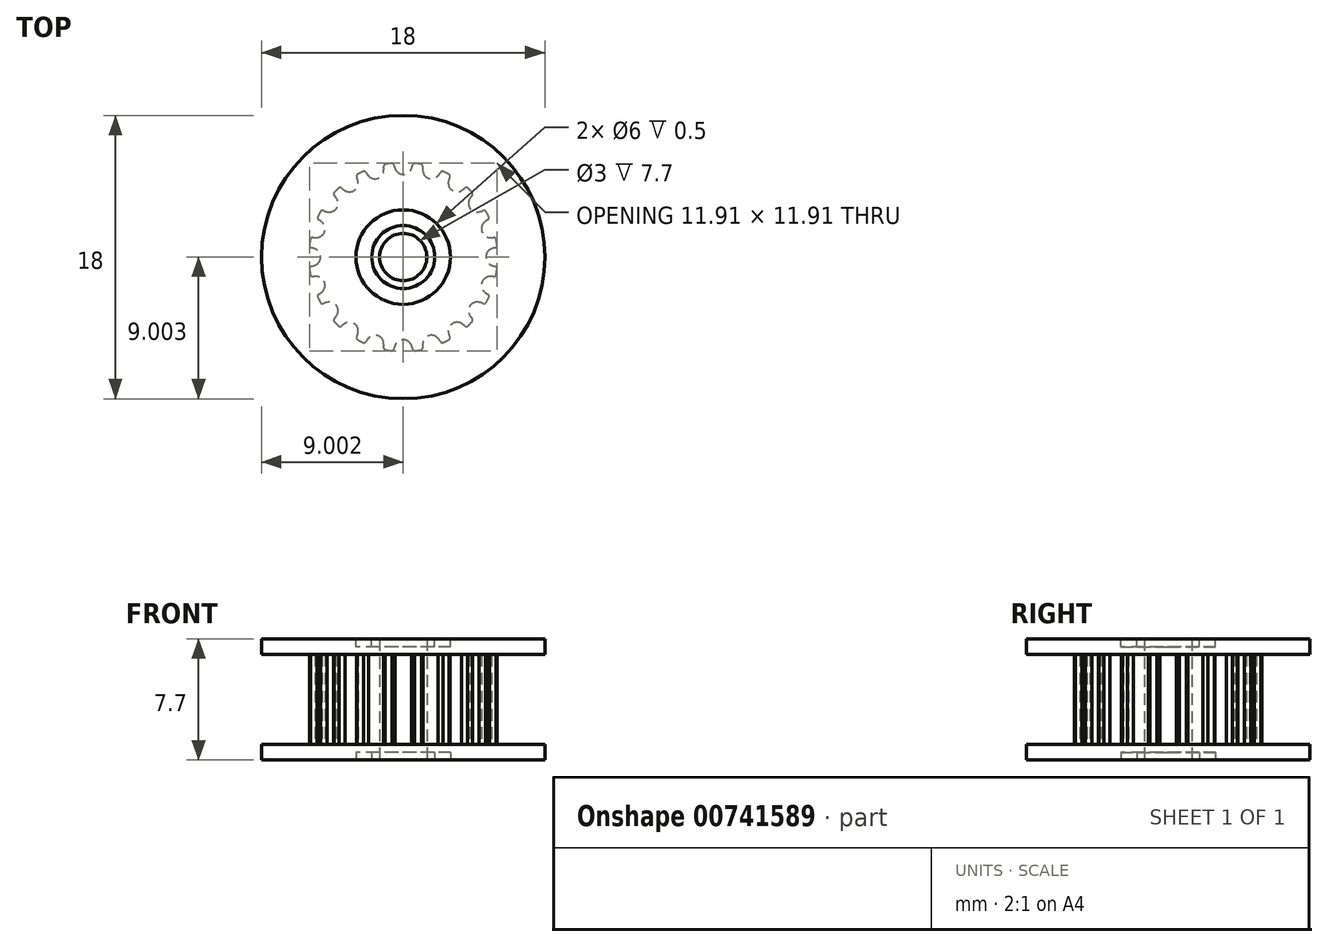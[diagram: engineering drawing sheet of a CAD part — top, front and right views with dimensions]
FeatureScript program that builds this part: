
annotation { "Feature Type Name" : "Feature", "Feature Type Description" : "" }
export const myFeature = defineFeature(function(context is Context, id is Id, definition is map)
    precondition{}
    {
        {
            var Q0;
            Q0=qCreatedBy(makeId("Top.planeOp"),FACE);
            var sketch = newSketch(context, id + "F0", { "sketchPlane" : qUnion([Q0])});
            skLineSegment(sketch, "E0", {"start": v(-17.44, 16.12) * mm, "end": v(-16.44, 16.12) * mm});
            skLineSegment(sketch, "E1", {"start": v(-16.44, 16.12) * mm, "end": v(-16.44, 16.75) * mm});
            skArc(sketch, "E2", {"start": v(-16.94, 17.19) * mm, "mid": v(-17.15, 17.42) * mm, "end": v(-17.44, 17.5) * mm});
            skArc(sketch, "E3", {"start": v(-16.85, 16.88) * mm, "mid": v(-16.88, 17.04) * mm, "end": v(-16.94, 17.19) * mm});
            skArc(sketch, "E4", {"start": v(-16.85, 16.88) * mm, "mid": v(-16.8, 16.79) * mm, "end": v(-16.7, 16.75) * mm});
            skLineSegment(sketch, "E5", {"start": v(-16.7, 16.75) * mm, "end": v(-16.44, 16.75) * mm});
            skArc(sketch, "E6.0.MirrorCS", {"start": v(-17.94, 17.19) * mm, "mid": v(-17.73, 17.42) * mm, "end": v(-17.44, 17.5) * mm});
            skArc(sketch, "E7.0.MirrorCS", {"start": v(-18.03, 16.88) * mm, "mid": v(-18, 17.04) * mm, "end": v(-17.94, 17.19) * mm});
            skArc(sketch, "E8.0.MirrorCS", {"start": v(-18.03, 16.88) * mm, "mid": v(-18.08, 16.79) * mm, "end": v(-18.18, 16.75) * mm});
            skLineSegment(sketch, "E9.0.MirrorCS", {"start": v(-18.18, 16.75) * mm, "end": v(-18.44, 16.75) * mm});
            skLineSegment(sketch, "E10.0.MirrorCS", {"start": v(-18.44, 16.12) * mm, "end": v(-18.44, 16.75) * mm});
            skLineSegment(sketch, "E11.0.MirrorCS", {"start": v(-17.44, 16.12) * mm, "end": v(-18.44, 16.12) * mm});
            skLineSegment(sketch, "E12.direction1", {"start": v(-18.44, 16.12) * mm, "end": v(-16.44, 16.12) * mm, "construction": true});
            skLineSegment(sketch, "E13", {"start": v(-18.44, 16.5) * mm, "end": v(-16.44, 16.5) * mm, "construction": true});
            skPoint(sketch, "E14", {"position": v(1.73, -6.9) * mm});
            skArc(sketch, "E15", {"start": v(2.25, -7.25) * mm, "mid": v(1.73, -6.9) * mm, "end": v(1.22, -7.25) * mm});
            skArc(sketch, "E16", {"start": v(1.22, -7.25) * mm, "mid": v(1.17, -7.37) * mm, "end": v(1.14, -7.5) * mm});
            skArc(sketch, "E17", {"start": v(2.32, -7.5) * mm, "mid": v(2.3, -7.37) * mm, "end": v(2.25, -7.25) * mm});
            skArc(sketch, "E18", {"start": v(2.45, -7.61) * mm, "mid": v(2.67, -7.58) * mm, "end": v(2.89, -7.54) * mm});
            skArc(sketch, "E19", {"start": v(2.32, -7.5) * mm, "mid": v(2.4, -7.6) * mm, "end": v(2.52, -7.6) * mm});
            skArc(sketch, "E20", {"start": v(1.14, -7.5) * mm, "mid": v(1.07, -7.6) * mm, "end": v(0.94, -7.6) * mm});
            skArc(sketch, "E21.1.0", {"start": v(3.95, -6.82) * mm, "mid": v(3.35, -6.65) * mm, "end": v(2.97, -7.14) * mm});
            skPoint(sketch, "E21.1.1", {"position": v(3.35, -6.65) * mm});
            skArc(sketch, "E21.1.2", {"start": v(2.97, -7.14) * mm, "mid": v(2.97, -7.26) * mm, "end": v(2.97, -7.39) * mm});
            skArc(sketch, "E21.1.3", {"start": v(4.1, -7.02) * mm, "mid": v(4.2, -7.1) * mm, "end": v(4.32, -7.07) * mm});
            skArc(sketch, "E21.1.4", {"start": v(2.97, -7.39) * mm, "mid": v(2.93, -7.51) * mm, "end": v(2.82, -7.56) * mm});
            skArc(sketch, "E21.1.5", {"start": v(4.1, -7.02) * mm, "mid": v(4.03, -6.92) * mm, "end": v(3.95, -6.82) * mm});
            skArc(sketch, "E22.3.2.0", {"start": v(5.44, -5.88) * mm, "mid": v(4.82, -5.9) * mm, "end": v(4.6, -6.49) * mm});
            skPoint(sketch, "E22.4.2.0", {"position": v(4.82, -5.9) * mm});
            skArc(sketch, "E22.5.2.0", {"start": v(4.6, -6.49) * mm, "mid": v(4.64, -6.6) * mm, "end": v(4.68, -6.72) * mm});
            skArc(sketch, "E22.9.2.0", {"start": v(5.64, -6.03) * mm, "mid": v(5.76, -6.07) * mm, "end": v(5.87, -6) * mm});
            skArc(sketch, "E22.13.2.0", {"start": v(4.68, -6.72) * mm, "mid": v(4.69, -6.85) * mm, "end": v(4.59, -6.93) * mm});
            skArc(sketch, "E22.17.2.0", {"start": v(5.64, -6.03) * mm, "mid": v(5.54, -5.95) * mm, "end": v(5.44, -5.88) * mm});
            skArc(sketch, "E22.3.3.0", {"start": v(6.56, -4.53) * mm, "mid": v(5.98, -4.74) * mm, "end": v(5.96, -5.36) * mm});
            skPoint(sketch, "E22.4.3.0", {"position": v(5.98, -4.74) * mm});
            skArc(sketch, "E22.5.3.0", {"start": v(5.96, -5.36) * mm, "mid": v(6.02, -5.47) * mm, "end": v(6.1, -5.56) * mm});
            skArc(sketch, "E22.9.3.0", {"start": v(6.8, -4.6) * mm, "mid": v(6.93, -4.61) * mm, "end": v(7, -4.51) * mm});
            skArc(sketch, "E22.13.3.0", {"start": v(6.1, -5.56) * mm, "mid": v(6.15, -5.69) * mm, "end": v(6.08, -5.8) * mm});
            skArc(sketch, "E22.17.3.0", {"start": v(6.8, -4.6) * mm, "mid": v(6.68, -4.56) * mm, "end": v(6.56, -4.53) * mm});
            skArc(sketch, "E22.3.4.0", {"start": v(7.21, -2.9) * mm, "mid": v(6.72, -3.28) * mm, "end": v(6.9, -3.87) * mm});
            skPoint(sketch, "E22.4.4.0", {"position": v(6.72, -3.28) * mm});
            skArc(sketch, "E22.5.4.0", {"start": v(6.9, -3.87) * mm, "mid": v(7, -3.95) * mm, "end": v(7.1, -4.02) * mm});
            skArc(sketch, "E22.9.4.0", {"start": v(7.46, -2.9) * mm, "mid": v(7.59, -2.86) * mm, "end": v(7.63, -2.74) * mm});
            skArc(sketch, "E22.13.4.0", {"start": v(7.1, -4.02) * mm, "mid": v(7.17, -4.12) * mm, "end": v(7.14, -4.25) * mm});
            skArc(sketch, "E22.17.4.0", {"start": v(7.46, -2.9) * mm, "mid": v(7.34, -2.9) * mm, "end": v(7.21, -2.9) * mm});
            skArc(sketch, "E22.3.5.0", {"start": v(7.33, -1.14) * mm, "mid": v(6.98, -1.66) * mm, "end": v(7.33, -2.17) * mm});
            skPoint(sketch, "E22.4.5.0", {"position": v(6.98, -1.66) * mm});
            skArc(sketch, "E22.5.5.0", {"start": v(7.33, -2.17) * mm, "mid": v(7.44, -2.22) * mm, "end": v(7.57, -2.25) * mm});
            skArc(sketch, "E22.9.5.0", {"start": v(7.57, -1.07) * mm, "mid": v(7.67, -1) * mm, "end": v(7.68, -0.86) * mm});
            skArc(sketch, "E22.13.5.0", {"start": v(7.57, -2.25) * mm, "mid": v(7.67, -2.32) * mm, "end": v(7.68, -2.45) * mm});
            skArc(sketch, "E22.17.5.0", {"start": v(7.57, -1.07) * mm, "mid": v(7.44, -1.1) * mm, "end": v(7.33, -1.14) * mm});
            skArc(sketch, "E22.3.6.0", {"start": v(6.9, 0.56) * mm, "mid": v(6.72, -0.03) * mm, "end": v(7.21, -0.42) * mm});
            skPoint(sketch, "E22.4.6.0", {"position": v(6.72, -0.03) * mm});
            skArc(sketch, "E22.5.6.0", {"start": v(7.21, -0.42) * mm, "mid": v(7.34, -0.42) * mm, "end": v(7.46, -0.41) * mm});
            skArc(sketch, "E22.9.6.0", {"start": v(7.1, 0.7) * mm, "mid": v(7.17, 0.81) * mm, "end": v(7.14, 0.93) * mm});
            skArc(sketch, "E22.13.6.0", {"start": v(7.46, -0.41) * mm, "mid": v(7.59, -0.45) * mm, "end": v(7.63, -0.57) * mm});
            skArc(sketch, "E22.17.6.0", {"start": v(7.1, 0.7) * mm, "mid": v(7, 0.64) * mm, "end": v(6.9, 0.56) * mm});
            skArc(sketch, "E22.3.7.0", {"start": v(5.96, 2.05) * mm, "mid": v(5.98, 1.43) * mm, "end": v(6.56, 1.22) * mm});
            skPoint(sketch, "E22.4.7.0", {"position": v(5.98, 1.43) * mm});
            skArc(sketch, "E22.5.7.0", {"start": v(6.56, 1.22) * mm, "mid": v(6.68, 1.25) * mm, "end": v(6.8, 1.3) * mm});
            skArc(sketch, "E22.9.7.0", {"start": v(6.1, 2.25) * mm, "mid": v(6.15, 2.37) * mm, "end": v(6.08, 2.48) * mm});
            skArc(sketch, "E22.13.7.0", {"start": v(6.8, 1.3) * mm, "mid": v(6.93, 1.3) * mm, "end": v(7, 1.2) * mm});
            skArc(sketch, "E22.17.7.0", {"start": v(6.1, 2.25) * mm, "mid": v(6.02, 2.15) * mm, "end": v(5.96, 2.05) * mm});
            skArc(sketch, "E22.3.8.0", {"start": v(4.6, 3.17) * mm, "mid": v(4.82, 2.6) * mm, "end": v(5.44, 2.57) * mm});
            skPoint(sketch, "E22.4.8.0", {"position": v(4.82, 2.6) * mm});
            skArc(sketch, "E22.5.8.0", {"start": v(5.44, 2.57) * mm, "mid": v(5.54, 2.64) * mm, "end": v(5.64, 2.72) * mm});
            skArc(sketch, "E22.9.8.0", {"start": v(4.68, 3.41) * mm, "mid": v(4.69, 3.54) * mm, "end": v(4.59, 3.62) * mm});
            skArc(sketch, "E22.13.8.0", {"start": v(5.64, 2.72) * mm, "mid": v(5.76, 2.76) * mm, "end": v(5.87, 2.69) * mm});
            skArc(sketch, "E22.17.8.0", {"start": v(4.68, 3.41) * mm, "mid": v(4.64, 3.3) * mm, "end": v(4.6, 3.17) * mm});
            skArc(sketch, "E22.3.9.0", {"start": v(2.97, 3.82) * mm, "mid": v(3.35, 3.34) * mm, "end": v(3.95, 3.5) * mm});
            skPoint(sketch, "E22.4.9.0", {"position": v(3.35, 3.34) * mm});
            skArc(sketch, "E22.5.9.0", {"start": v(3.95, 3.5) * mm, "mid": v(4.03, 3.6) * mm, "end": v(4.1, 3.71) * mm});
            skArc(sketch, "E22.9.9.0", {"start": v(2.97, 4.07) * mm, "mid": v(2.93, 4.2) * mm, "end": v(2.82, 4.24) * mm});
            skArc(sketch, "E22.13.9.0", {"start": v(4.1, 3.71) * mm, "mid": v(4.2, 3.79) * mm, "end": v(4.32, 3.75) * mm});
            skArc(sketch, "E22.17.9.0", {"start": v(2.97, 4.07) * mm, "mid": v(2.97, 3.95) * mm, "end": v(2.97, 3.82) * mm});
            skArc(sketch, "E22.3.10.0", {"start": v(1.22, 3.94) * mm, "mid": v(1.73, 3.6) * mm, "end": v(2.25, 3.94) * mm});
            skPoint(sketch, "E22.4.10.0", {"position": v(1.73, 3.6) * mm});
            skArc(sketch, "E22.5.10.0", {"start": v(2.25, 3.94) * mm, "mid": v(2.3, 4.06) * mm, "end": v(2.32, 4.18) * mm});
            skArc(sketch, "E22.9.10.0", {"start": v(1.14, 4.18) * mm, "mid": v(1.07, 4.28) * mm, "end": v(0.94, 4.3) * mm});
            skArc(sketch, "E22.13.10.0", {"start": v(2.32, 4.18) * mm, "mid": v(2.4, 4.28) * mm, "end": v(2.52, 4.3) * mm});
            skArc(sketch, "E22.17.10.0", {"start": v(1.14, 4.18) * mm, "mid": v(1.17, 4.06) * mm, "end": v(1.22, 3.94) * mm});
            skArc(sketch, "E22.3.11.0", {"start": v(-0.49, 3.5) * mm, "mid": v(0.1, 3.34) * mm, "end": v(0.5, 3.82) * mm});
            skPoint(sketch, "E22.4.11.0", {"position": v(0.1, 3.34) * mm});
            skArc(sketch, "E22.5.11.0", {"start": v(0.5, 3.82) * mm, "mid": v(0.5, 3.95) * mm, "end": v(0.49, 4.07) * mm});
            skArc(sketch, "E22.9.11.0", {"start": v(-0.63, 3.71) * mm, "mid": v(-0.74, 3.79) * mm, "end": v(-0.86, 3.75) * mm});
            skArc(sketch, "E22.13.11.0", {"start": v(0.49, 4.07) * mm, "mid": v(0.53, 4.2) * mm, "end": v(0.65, 4.24) * mm});
            skArc(sketch, "E22.17.11.0", {"start": v(-0.63, 3.71) * mm, "mid": v(-0.57, 3.6) * mm, "end": v(-0.49, 3.5) * mm});
            skArc(sketch, "E22.3.12.0", {"start": v(-1.97, 2.57) * mm, "mid": v(-1.35, 2.6) * mm, "end": v(-1.14, 3.17) * mm});
            skPoint(sketch, "E22.4.12.0", {"position": v(-1.35, 2.6) * mm});
            skArc(sketch, "E22.5.12.0", {"start": v(-1.14, 3.17) * mm, "mid": v(-1.17, 3.3) * mm, "end": v(-1.22, 3.41) * mm});
            skArc(sketch, "E22.9.12.0", {"start": v(-2.18, 2.72) * mm, "mid": v(-2.3, 2.76) * mm, "end": v(-2.4, 2.69) * mm});
            skArc(sketch, "E22.13.12.0", {"start": v(-1.22, 3.41) * mm, "mid": v(-1.22, 3.54) * mm, "end": v(-1.12, 3.62) * mm});
            skArc(sketch, "E22.17.12.0", {"start": v(-2.18, 2.72) * mm, "mid": v(-2.08, 2.64) * mm, "end": v(-1.97, 2.57) * mm});
            skArc(sketch, "E22.3.13.0", {"start": v(-3.1, 1.22) * mm, "mid": v(-2.52, 1.43) * mm, "end": v(-2.5, 2.05) * mm});
            skPoint(sketch, "E22.4.13.0", {"position": v(-2.52, 1.43) * mm});
            skArc(sketch, "E22.5.13.0", {"start": v(-2.5, 2.05) * mm, "mid": v(-2.56, 2.15) * mm, "end": v(-2.64, 2.25) * mm});
            skArc(sketch, "E22.9.13.0", {"start": v(-3.34, 1.3) * mm, "mid": v(-3.46, 1.3) * mm, "end": v(-3.55, 1.2) * mm});
            skArc(sketch, "E22.13.13.0", {"start": v(-2.64, 2.25) * mm, "mid": v(-2.68, 2.37) * mm, "end": v(-2.61, 2.48) * mm});
            skArc(sketch, "E22.17.13.0", {"start": v(-3.34, 1.3) * mm, "mid": v(-3.22, 1.25) * mm, "end": v(-3.1, 1.22) * mm});
            skArc(sketch, "E22.3.14.0", {"start": v(-3.75, -0.42) * mm, "mid": v(-3.26, -0.03) * mm, "end": v(-3.43, 0.56) * mm});
            skPoint(sketch, "E22.4.14.0", {"position": v(-3.26, -0.03) * mm});
            skArc(sketch, "E22.5.14.0", {"start": v(-3.43, 0.56) * mm, "mid": v(-3.53, 0.64) * mm, "end": v(-3.64, 0.7) * mm});
            skArc(sketch, "E22.9.14.0", {"start": v(-4, -0.41) * mm, "mid": v(-4.12, -0.45) * mm, "end": v(-4.17, -0.57) * mm});
            skArc(sketch, "E22.13.14.0", {"start": v(-3.64, 0.7) * mm, "mid": v(-3.71, 0.81) * mm, "end": v(-3.68, 0.93) * mm});
            skArc(sketch, "E22.17.14.0", {"start": v(-4, -0.41) * mm, "mid": v(-3.87, -0.42) * mm, "end": v(-3.75, -0.42) * mm});
            skArc(sketch, "E22.3.15.0", {"start": v(-3.86, -2.17) * mm, "mid": v(-3.52, -1.66) * mm, "end": v(-3.86, -1.14) * mm});
            skPoint(sketch, "E22.4.15.0", {"position": v(-3.52, -1.66) * mm});
            skArc(sketch, "E22.5.15.0", {"start": v(-3.86, -1.14) * mm, "mid": v(-3.98, -1.1) * mm, "end": v(-4.1, -1.07) * mm});
            skArc(sketch, "E22.9.15.0", {"start": v(-4.1, -2.25) * mm, "mid": v(-4.2, -2.32) * mm, "end": v(-4.22, -2.45) * mm});
            skArc(sketch, "E22.13.15.0", {"start": v(-4.1, -1.07) * mm, "mid": v(-4.2, -1) * mm, "end": v(-4.22, -0.86) * mm});
            skArc(sketch, "E22.17.15.0", {"start": v(-4.1, -2.25) * mm, "mid": v(-3.98, -2.22) * mm, "end": v(-3.86, -2.17) * mm});
            skArc(sketch, "E22.3.16.0", {"start": v(-3.43, -3.87) * mm, "mid": v(-3.26, -3.28) * mm, "end": v(-3.75, -2.9) * mm});
            skPoint(sketch, "E22.4.16.0", {"position": v(-3.26, -3.28) * mm});
            skArc(sketch, "E22.5.16.0", {"start": v(-3.75, -2.9) * mm, "mid": v(-3.87, -2.9) * mm, "end": v(-4, -2.9) * mm});
            skArc(sketch, "E22.9.16.0", {"start": v(-3.64, -4.02) * mm, "mid": v(-3.71, -4.12) * mm, "end": v(-3.68, -4.25) * mm});
            skArc(sketch, "E22.13.16.0", {"start": v(-4, -2.9) * mm, "mid": v(-4.12, -2.86) * mm, "end": v(-4.17, -2.74) * mm});
            skArc(sketch, "E22.17.16.0", {"start": v(-3.64, -4.02) * mm, "mid": v(-3.53, -3.95) * mm, "end": v(-3.43, -3.87) * mm});
            skArc(sketch, "E22.3.17.0", {"start": v(-2.5, -5.36) * mm, "mid": v(-2.52, -4.74) * mm, "end": v(-3.1, -4.53) * mm});
            skPoint(sketch, "E22.4.17.0", {"position": v(-2.52, -4.74) * mm});
            skArc(sketch, "E22.5.17.0", {"start": v(-3.1, -4.53) * mm, "mid": v(-3.22, -4.56) * mm, "end": v(-3.34, -4.6) * mm});
            skArc(sketch, "E22.9.17.0", {"start": v(-2.64, -5.56) * mm, "mid": v(-2.68, -5.69) * mm, "end": v(-2.61, -5.8) * mm});
            skArc(sketch, "E22.13.17.0", {"start": v(-3.34, -4.6) * mm, "mid": v(-3.46, -4.61) * mm, "end": v(-3.55, -4.51) * mm});
            skArc(sketch, "E22.17.17.0", {"start": v(-2.64, -5.56) * mm, "mid": v(-2.56, -5.47) * mm, "end": v(-2.5, -5.36) * mm});
            skArc(sketch, "E22.3.18.0", {"start": v(-1.14, -6.49) * mm, "mid": v(-1.35, -5.9) * mm, "end": v(-1.97, -5.88) * mm});
            skPoint(sketch, "E22.4.18.0", {"position": v(-1.35, -5.9) * mm});
            skArc(sketch, "E22.5.18.0", {"start": v(-1.97, -5.88) * mm, "mid": v(-2.08, -5.95) * mm, "end": v(-2.18, -6.03) * mm});
            skArc(sketch, "E22.9.18.0", {"start": v(-1.22, -6.72) * mm, "mid": v(-1.22, -6.85) * mm, "end": v(-1.12, -6.93) * mm});
            skArc(sketch, "E22.13.18.0", {"start": v(-2.18, -6.03) * mm, "mid": v(-2.3, -6.07) * mm, "end": v(-2.4, -6) * mm});
            skArc(sketch, "E22.17.18.0", {"start": v(-1.22, -6.72) * mm, "mid": v(-1.17, -6.6) * mm, "end": v(-1.14, -6.49) * mm});
            skArc(sketch, "E22.3.19.0", {"start": v(0.5, -7.14) * mm, "mid": v(0.1, -6.65) * mm, "end": v(-0.49, -6.82) * mm});
            skPoint(sketch, "E22.4.19.0", {"position": v(0.1, -6.65) * mm});
            skArc(sketch, "E22.5.19.0", {"start": v(-0.49, -6.82) * mm, "mid": v(-0.57, -6.92) * mm, "end": v(-0.63, -7.02) * mm});
            skArc(sketch, "E22.9.19.0", {"start": v(0.49, -7.39) * mm, "mid": v(0.53, -7.51) * mm, "end": v(0.65, -7.56) * mm});
            skArc(sketch, "E22.13.19.0", {"start": v(-0.63, -7.02) * mm, "mid": v(-0.74, -7.1) * mm, "end": v(-0.86, -7.07) * mm});
            skArc(sketch, "E22.17.19.0", {"start": v(0.49, -7.39) * mm, "mid": v(0.5, -7.26) * mm, "end": v(0.5, -7.14) * mm});
            skArc(sketch, "E23.trimOffspring", {"start": v(4.26, -7.1) * mm, "mid": v(4.46, -7) * mm, "end": v(4.65, -6.9) * mm});
            skArc(sketch, "E24.trimOffspring", {"start": v(5.81, -6.05) * mm, "mid": v(5.97, -5.9) * mm, "end": v(6.13, -5.74) * mm});
            skArc(sketch, "E25.trimOffspring", {"start": v(6.97, -4.58) * mm, "mid": v(7.06, -4.41) * mm, "end": v(7.14, -4.25) * mm});
            skArc(sketch, "E26.trimOffspring", {"start": v(7.62, -2.81) * mm, "mid": v(7.66, -2.6) * mm, "end": v(7.69, -2.38) * mm});
            skArc(sketch, "E27.trimOffspring", {"start": v(7.18, 0.87) * mm, "mid": v(7.08, 1.07) * mm, "end": v(6.97, 1.26) * mm});
            skArc(sketch, "E28.trimOffspring", {"start": v(6.13, 2.43) * mm, "mid": v(5.97, 2.59) * mm, "end": v(5.81, 2.74) * mm});
            skArc(sketch, "E29.trimOffspring", {"start": v(7.69, -0.94) * mm, "mid": v(7.66, -0.72) * mm, "end": v(7.62, -0.5) * mm});
            skArc(sketch, "E30.trimOffspring", {"start": v(4.65, 3.58) * mm, "mid": v(4.46, 3.69) * mm, "end": v(4.26, 3.79) * mm});
            skArc(sketch, "E31.trimOffspring", {"start": v(2.89, 4.23) * mm, "mid": v(2.67, 4.27) * mm, "end": v(2.45, 4.3) * mm});
            skArc(sketch, "E32.trimOffspring", {"start": v(1.01, 4.3) * mm, "mid": v(0.8, 4.27) * mm, "end": v(0.57, 4.23) * mm});
            skArc(sketch, "E33.trimOffspring", {"start": v(-0.8, 3.79) * mm, "mid": v(-1, 3.69) * mm, "end": v(-1.19, 3.58) * mm});
            skArc(sketch, "E34.trimOffspring", {"start": v(-2.35, 2.74) * mm, "mid": v(-2.51, 2.59) * mm, "end": v(-2.67, 2.43) * mm});
            skArc(sketch, "E35.trimOffspring", {"start": v(-3.5, 1.26) * mm, "mid": v(-3.61, 1.07) * mm, "end": v(-3.71, 0.87) * mm});
            skArc(sketch, "E36.trimOffspring", {"start": v(-4.16, -0.5) * mm, "mid": v(-4.2, -0.72) * mm, "end": v(-4.23, -0.94) * mm});
            skArc(sketch, "E37.trimOffspring", {"start": v(-4.23, -2.38) * mm, "mid": v(-4.2, -2.6) * mm, "end": v(-4.16, -2.81) * mm});
            skArc(sketch, "E38.trimOffspring", {"start": v(-3.71, -4.18) * mm, "mid": v(-3.61, -4.38) * mm, "end": v(-3.5, -4.58) * mm});
            skArc(sketch, "E39.trimOffspring", {"start": v(-2.67, -5.74) * mm, "mid": v(-2.51, -5.9) * mm, "end": v(-2.35, -6.05) * mm});
            skArc(sketch, "E40.trimOffspring", {"start": v(-1.19, -6.9) * mm, "mid": v(-1, -7) * mm, "end": v(-0.8, -7.1) * mm});
            skArc(sketch, "E41.trimOffspring", {"start": v(0.57, -7.54) * mm, "mid": v(0.8, -7.58) * mm, "end": v(1.01, -7.61) * mm});
            skSolve(sketch);
        }
        {
            var Q0;
            Q0=makeQuery(id+"F0.imprint","IMPRINT",FACE,{"disambiguationData":[TD([[makeQuery(id+"F0.imprint","IMPRINT",EDGE,{"derivedFrom":sQuery(id+"F0.wireOp",EDGE,"E15")}),-1.0]])]});
            var sketch = newSketch(context, id + "F1", { "sketchPlane" : qUnion([Q0])});
            skPoint(sketch, "E42.0", {"position": v(1.73, -1.66) * mm});
            skCircle(sketch, "E43", {"center": v(1.73, -1.66) * mm, "radius": 1.5 * mm});
            skCircle(sketch, "E44", {"center": v(1.73, -1.66) * mm, "radius": 2 * mm});
            skCircle(sketch, "E45", {"center": v(1.73, -1.66) * mm, "radius": 3 * mm});
            skSolve(sketch);
        }
        {
            var Q0;
            Q0=makeQuery(id+"F0.imprint","IMPRINT",FACE,{"disambiguationData":[TD([[makeQuery(id+"F0.imprint","IMPRINT",EDGE,{"derivedFrom":sQuery(id+"F0.wireOp",EDGE,"E15")}),-1.0]])]});
            extrude(context, id + "F2", {"entities" : qUnion([Q0]), "depth" : 6.7 * mm, "offsetDistance" : 25.4 * mm});
        }
        {
            var Q0;
            Q0=makeQuery(id+"F2.opExtrude","CAP_FACE",FACE,{"disambiguationData":[OSD([sQuery(id+"F0.wireOp",EDGE,"E15"),sQuery(id+"F0.wireOp",EDGE,"E16"),sQuery(id+"F0.wireOp",EDGE,"E17"),sQuery(id+"F0.wireOp",EDGE,"E18"),sQuery(id+"F0.wireOp",EDGE,"E19"),sQuery(id+"F0.wireOp",EDGE,"E20"),sQuery(id+"F0.wireOp",EDGE,"E21.1.0"),sQuery(id+"F0.wireOp",EDGE,"E21.1.2"),sQuery(id+"F0.wireOp",EDGE,"E21.1.3"),sQuery(id+"F0.wireOp",EDGE,"E21.1.4"),sQuery(id+"F0.wireOp",EDGE,"E21.1.5"),sQuery(id+"F0.wireOp",EDGE,"E22.3.2.0"),sQuery(id+"F0.wireOp",EDGE,"E22.5.2.0"),sQuery(id+"F0.wireOp",EDGE,"E22.9.2.0"),sQuery(id+"F0.wireOp",EDGE,"E22.13.2.0"),sQuery(id+"F0.wireOp",EDGE,"E22.17.2.0"),sQuery(id+"F0.wireOp",EDGE,"E22.3.3.0"),sQuery(id+"F0.wireOp",EDGE,"E22.5.3.0"),sQuery(id+"F0.wireOp",EDGE,"E22.9.3.0"),sQuery(id+"F0.wireOp",EDGE,"E22.13.3.0"),sQuery(id+"F0.wireOp",EDGE,"E22.17.3.0"),sQuery(id+"F0.wireOp",EDGE,"E22.3.4.0"),sQuery(id+"F0.wireOp",EDGE,"E22.5.4.0"),sQuery(id+"F0.wireOp",EDGE,"E22.9.4.0"),sQuery(id+"F0.wireOp",EDGE,"E22.13.4.0"),sQuery(id+"F0.wireOp",EDGE,"E22.17.4.0"),sQuery(id+"F0.wireOp",EDGE,"E22.3.5.0"),sQuery(id+"F0.wireOp",EDGE,"E22.5.5.0"),sQuery(id+"F0.wireOp",EDGE,"E22.9.5.0"),sQuery(id+"F0.wireOp",EDGE,"E22.13.5.0"),sQuery(id+"F0.wireOp",EDGE,"E22.17.5.0"),sQuery(id+"F0.wireOp",EDGE,"E22.3.6.0"),sQuery(id+"F0.wireOp",EDGE,"E22.5.6.0"),sQuery(id+"F0.wireOp",EDGE,"E22.9.6.0"),sQuery(id+"F0.wireOp",EDGE,"E22.13.6.0"),sQuery(id+"F0.wireOp",EDGE,"E22.17.6.0"),sQuery(id+"F0.wireOp",EDGE,"E22.3.7.0"),sQuery(id+"F0.wireOp",EDGE,"E22.5.7.0"),sQuery(id+"F0.wireOp",EDGE,"E22.9.7.0"),sQuery(id+"F0.wireOp",EDGE,"E22.13.7.0"),sQuery(id+"F0.wireOp",EDGE,"E22.17.7.0"),sQuery(id+"F0.wireOp",EDGE,"E22.3.8.0"),sQuery(id+"F0.wireOp",EDGE,"E22.5.8.0"),sQuery(id+"F0.wireOp",EDGE,"E22.9.8.0"),sQuery(id+"F0.wireOp",EDGE,"E22.13.8.0"),sQuery(id+"F0.wireOp",EDGE,"E22.17.8.0"),sQuery(id+"F0.wireOp",EDGE,"E22.3.9.0"),sQuery(id+"F0.wireOp",EDGE,"E22.5.9.0"),sQuery(id+"F0.wireOp",EDGE,"E22.9.9.0"),sQuery(id+"F0.wireOp",EDGE,"E22.13.9.0"),sQuery(id+"F0.wireOp",EDGE,"E22.17.9.0"),sQuery(id+"F0.wireOp",EDGE,"E22.3.10.0"),sQuery(id+"F0.wireOp",EDGE,"E22.5.10.0"),sQuery(id+"F0.wireOp",EDGE,"E22.9.10.0"),sQuery(id+"F0.wireOp",EDGE,"E22.13.10.0"),sQuery(id+"F0.wireOp",EDGE,"E22.17.10.0"),sQuery(id+"F0.wireOp",EDGE,"E22.3.11.0"),sQuery(id+"F0.wireOp",EDGE,"E22.5.11.0"),sQuery(id+"F0.wireOp",EDGE,"E22.9.11.0"),sQuery(id+"F0.wireOp",EDGE,"E22.13.11.0"),sQuery(id+"F0.wireOp",EDGE,"E22.17.11.0"),sQuery(id+"F0.wireOp",EDGE,"E22.3.12.0"),sQuery(id+"F0.wireOp",EDGE,"E22.5.12.0"),sQuery(id+"F0.wireOp",EDGE,"E22.9.12.0"),sQuery(id+"F0.wireOp",EDGE,"E22.13.12.0"),sQuery(id+"F0.wireOp",EDGE,"E22.17.12.0"),sQuery(id+"F0.wireOp",EDGE,"E22.3.13.0"),sQuery(id+"F0.wireOp",EDGE,"E22.5.13.0"),sQuery(id+"F0.wireOp",EDGE,"E22.9.13.0"),sQuery(id+"F0.wireOp",EDGE,"E22.13.13.0"),sQuery(id+"F0.wireOp",EDGE,"E22.17.13.0"),sQuery(id+"F0.wireOp",EDGE,"E22.3.14.0"),sQuery(id+"F0.wireOp",EDGE,"E22.5.14.0"),sQuery(id+"F0.wireOp",EDGE,"E22.9.14.0"),sQuery(id+"F0.wireOp",EDGE,"E22.13.14.0"),sQuery(id+"F0.wireOp",EDGE,"E22.17.14.0"),sQuery(id+"F0.wireOp",EDGE,"E22.3.15.0"),sQuery(id+"F0.wireOp",EDGE,"E22.5.15.0"),sQuery(id+"F0.wireOp",EDGE,"E22.9.15.0"),sQuery(id+"F0.wireOp",EDGE,"E22.13.15.0"),sQuery(id+"F0.wireOp",EDGE,"E22.17.15.0"),sQuery(id+"F0.wireOp",EDGE,"E22.3.16.0"),sQuery(id+"F0.wireOp",EDGE,"E22.5.16.0"),sQuery(id+"F0.wireOp",EDGE,"E22.9.16.0"),sQuery(id+"F0.wireOp",EDGE,"E22.13.16.0"),sQuery(id+"F0.wireOp",EDGE,"E22.17.16.0"),sQuery(id+"F0.wireOp",EDGE,"E22.3.17.0"),sQuery(id+"F0.wireOp",EDGE,"E22.5.17.0"),sQuery(id+"F0.wireOp",EDGE,"E22.9.17.0"),sQuery(id+"F0.wireOp",EDGE,"E22.13.17.0"),sQuery(id+"F0.wireOp",EDGE,"E22.17.17.0"),sQuery(id+"F0.wireOp",EDGE,"E22.3.18.0"),sQuery(id+"F0.wireOp",EDGE,"E22.5.18.0"),sQuery(id+"F0.wireOp",EDGE,"E22.9.18.0"),sQuery(id+"F0.wireOp",EDGE,"E22.13.18.0"),sQuery(id+"F0.wireOp",EDGE,"E22.17.18.0"),sQuery(id+"F0.wireOp",EDGE,"E22.3.19.0"),sQuery(id+"F0.wireOp",EDGE,"E22.5.19.0"),sQuery(id+"F0.wireOp",EDGE,"E22.9.19.0"),sQuery(id+"F0.wireOp",EDGE,"E22.13.19.0"),sQuery(id+"F0.wireOp",EDGE,"E22.17.19.0"),sQuery(id+"F0.wireOp",EDGE,"E23.trimOffspring"),sQuery(id+"F0.wireOp",EDGE,"E24.trimOffspring"),sQuery(id+"F0.wireOp",EDGE,"E25.trimOffspring"),sQuery(id+"F0.wireOp",EDGE,"E26.trimOffspring"),sQuery(id+"F0.wireOp",EDGE,"E27.trimOffspring"),sQuery(id+"F0.wireOp",EDGE,"E28.trimOffspring"),sQuery(id+"F0.wireOp",EDGE,"E29.trimOffspring"),sQuery(id+"F0.wireOp",EDGE,"E30.trimOffspring"),sQuery(id+"F0.wireOp",EDGE,"E31.trimOffspring"),sQuery(id+"F0.wireOp",EDGE,"E32.trimOffspring"),sQuery(id+"F0.wireOp",EDGE,"E33.trimOffspring"),sQuery(id+"F0.wireOp",EDGE,"E34.trimOffspring"),sQuery(id+"F0.wireOp",EDGE,"E35.trimOffspring"),sQuery(id+"F0.wireOp",EDGE,"E36.trimOffspring"),sQuery(id+"F0.wireOp",EDGE,"E37.trimOffspring"),sQuery(id+"F0.wireOp",EDGE,"E38.trimOffspring"),sQuery(id+"F0.wireOp",EDGE,"E39.trimOffspring"),sQuery(id+"F0.wireOp",EDGE,"E40.trimOffspring"),sQuery(id+"F0.wireOp",EDGE,"E41.trimOffspring")])],"isStart":false});
            var sketch = newSketch(context, id + "F3", { "sketchPlane" : qUnion([Q0])});
            skCircle(sketch, "E46", {"center": v(1.73, -1.66) * mm, "radius": 9 * mm});
            skSolve(sketch);
        }
        {
            var Q0;
            Q0=makeQuery(id+"F3.imprint","IMPRINT",FACE,{"disambiguationData":[TD([[makeQuery(id+"F3.imprint","IMPRINT",EDGE,{"derivedFrom":sQuery(id+"F3.wireOp",EDGE,"E46")}),1.0]])]});
            var Q1;
            Q1=makeQuery(id+"F3.imprint","IMPRINT",FACE,{"disambiguationData":[TD([[makeQuery(id+"F3.imprint","IMPRINT",EDGE,{"derivedFrom":makeQuery(id+"F2.opExtrude","CAP_EDGE",EDGE,{"disambiguationData":[OSD([sQuery(id+"F0.wireOp",EDGE,"E15")])],"isStart":false})}),-1.0]])]});
            extrude(context, id + "F4", {"entities" : qUnion([Q0, Q1]), "operationType" : NewBodyOperationType.ADD, "depth" : 1 * mm, "offsetDistance" : 25 * mm});
        }
        {
            var Q0;
            Q0=makeQuery(id+"F0.imprint","IMPRINT",FACE,{"disambiguationData":[TD([[makeQuery(id+"F0.imprint","IMPRINT",EDGE,{"derivedFrom":sQuery(id+"F0.wireOp",EDGE,"E15")}),-1.0]])]});
            var sketch = newSketch(context, id + "F5", { "sketchPlane" : qUnion([Q0])});
            skPoint(sketch, "E47.0", {"position": v(1.73, -1.66) * mm});
            skCircle(sketch, "E48", {"center": v(1.73, -1.66) * mm, "radius": 9 * mm});
            skSolve(sketch);
        }
        {
            var Q0;
            Q0=makeQuery(id+"F5.imprint","IMPRINT",FACE,{"disambiguationData":[TD([[makeQuery(id+"F5.imprint","IMPRINT",EDGE,{"derivedFrom":sQuery(id+"F5.wireOp",EDGE,"E48")}),1.0]])]});
            var Q1;
            Q1=makeQuery(id+"F0.imprint","IMPRINT",FACE,{"disambiguationData":[TD([[makeQuery(id+"F0.imprint","IMPRINT",EDGE,{"derivedFrom":sQuery(id+"F0.wireOp",EDGE,"E15")}),-1.0]])]});
            extrude(context, id + "F6", {"entities" : qUnion([Q0, Q1]), "operationType" : NewBodyOperationType.ADD, "depth" : 1 * mm, "offsetDistance" : 25 * mm});
        }
        {
            var Q0;
            Q0=makeQuery(id+"F1.imprint","IMPRINT",FACE,{"disambiguationData":[TD([[makeQuery(id+"F1.imprint","IMPRINT",EDGE,{"derivedFrom":sQuery(id+"F1.wireOp",EDGE,"E43")}),1.0]])]});
            extrude(context, id + "F7", {"entities" : qUnion([Q0]), "operationType" : NewBodyOperationType.REMOVE, "endBound" : BoundingType.THROUGH_ALL, "depth" : 25 * mm, "offsetDistance" : 25 * mm});
        }
        {
            var Q0;
            Q0=makeQuery(id+"F1.imprint","IMPRINT",FACE,{"disambiguationData":[TD([[makeQuery(id+"F1.imprint","IMPRINT",EDGE,{"derivedFrom":sQuery(id+"F1.wireOp",EDGE,"E44")}),-1.0]])]});
            extrude(context, id + "F8", {"entities" : qUnion([Q0]), "operationType" : NewBodyOperationType.REMOVE, "depth" : .5 * mm, "offsetDistance" : 25 * mm});
        }
        {
            var Q0;
            Q0=makeQuery(id+"F4.opExtrude","CAP_FACE",FACE,{"disambiguationData":[OSD([sQuery(id+"F3.wireOp",EDGE,"E46")])],"isStart":false});
            var sketch = newSketch(context, id + "F9", { "sketchPlane" : qUnion([Q0])});
            skCircle(sketch, "E49.0", {"center": v(1.73, -1.66) * mm, "radius": 3 * mm});
            skCircle(sketch, "E50.0", {"center": v(1.73, -1.66) * mm, "radius": 2 * mm});
            skSolve(sketch);
        }
        {
            var Q0;
            Q0=makeQuery(id+"F9.imprint","IMPRINT",FACE,{"disambiguationData":[TD([[makeQuery(id+"F9.imprint","IMPRINT",EDGE,{"derivedFrom":sQuery(id+"F9.wireOp",EDGE,"E49.0")}),1.0]])]});
            extrude(context, id + "F10", {"entities" : qUnion([Q0]), "operationType" : NewBodyOperationType.REMOVE, "oppositeDirection" : true, "depth" : .5 * mm, "offsetDistance" : 25 * mm});
        }
    });
